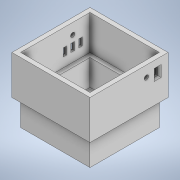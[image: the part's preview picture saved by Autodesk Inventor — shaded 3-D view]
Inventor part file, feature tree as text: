
AUTODESK INVENTOR PART (.ipt)
format: ipt  version: 2020 (Build 240168000, 168)  size: 198,656 bytes
history: native  units: in
note: dims shown in document units (in); Inventor stores cm internally (conversion verified against a paired STEP export)
features: extrude x7, sketch x7, chamfer x2
ambient origin geometry x8: Origin, YZ Plane, XZ Plane, XY Plane, X Axis, Y Axis, Z Axis, Center Point
bodies: Solid1 (feature_tree)
feature tree (16):
  extrude  "Extrusion1"  Depth=3.1496in
  extrude  "Extrusion2"  Depth=0.1969in
  extrude  "Extrusion3"  Depth=0.1969in
  extrude  "Extrusion4"  Depth=1.7717in TaperAngle=0.0deg
  extrude  "Extrusion5"  Depth=0.1969in
  extrude  "Extrusion6"  Depth=0.1969in
  chamfer  "Chamfer1"  Distance=0.1969in
  extrude  "Extrusion7"  Depth=0.1969in
  chamfer  "Chamfer2"  Distance=1.1811in
  sketch  "Sketch1"  dims[d0=3.1496in d1=3.1496in]
  sketch  "Sketch2"  dims[d2=1.1811in d3=0.0in d4=0.1969in]
  sketch  "Sketch3"  dims[d5=0.1969in d6=0.1969in]
  sketch  "Sketch4"  dims[d7=0.1969in d8=1.7717in d9=0.0in]
  sketch  "Sketch5"  dims[d10=0.1969in d11=0.1969in]
  sketch  "Sketch6"  dims[d12=1.5748in d13=0.0in d14=0.1969in]
  sketch  "Sketch8"  dims[d15=0.1969in d16=0.1969in d17=0.1969in d18=1.1811in d19=0.0in d20=0.1969in d21=0.4921in d22=0.9843in d23=0.3937in d24=0.0in d25=0.3937in d26=0.1575in d27=0.3543in d28=0.3937in d29=0.3937in d30=0.0in d31=0.0787in d32=0.0787in d33=45.0deg d39=0.1575in d40=0.3543in d41=0.1575in d42=0.1575in d43=0.7874in d44=0.9055in d45=0.1969in d46=0.1969in d47=0.3937in d48=0.0in d49=0.0787in d50=0.0787in d51=45.0deg]
